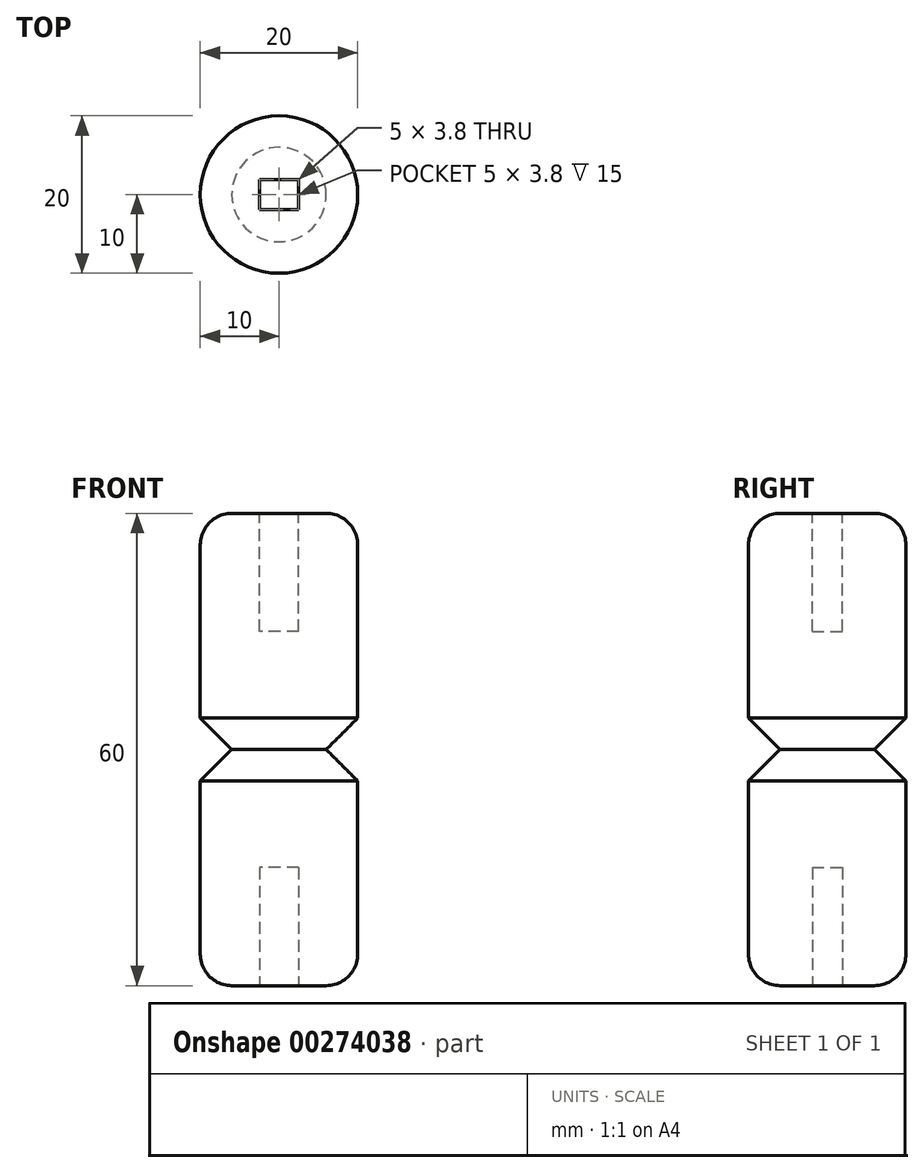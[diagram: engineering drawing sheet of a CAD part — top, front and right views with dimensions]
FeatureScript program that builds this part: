
annotation { "Feature Type Name" : "Feature", "Feature Type Description" : "" }
export const myFeature = defineFeature(function(context is Context, id is Id, definition is map)
    precondition{}
    {
        {
            var Q0;
            Q0=qCreatedBy(makeId("Top.planeOp"),FACE);
            var sketch = newSketch(context, id + "F0", { "sketchPlane" : qUnion([Q0])});
            skCircle(sketch, "E0", {"center": v(0, 0) * mm, "radius": 10 * mm});
            skSolve(sketch);
        }
        {
            var Q0;
            Q0 = qSketchRegion(id + "F0", true);
            extrude(context, id + "F1", {"entities" : qUnion([Q0]), "depth" : 30 * mm});
        }
        {
            var Q0;
            Q0=makeQuery(id+"F1.opExtrude","CAP_FACE",FACE,{"disambiguationData":[OSD([sQuery(id+"F0.wireOp",EDGE,"E0")])],"isStart":false});
            var sketch = newSketch(context, id + "F2", { "sketchPlane" : qUnion([Q0])});
            skLineSegment(sketch, "E1.bottom", {"start": v(2.5, -1.9) * mm, "end": v(-2.5, -1.9) * mm});
            skLineSegment(sketch, "E1.top", {"start": v(2.5, 1.9) * mm, "end": v(-2.5, 1.9) * mm});
            skLineSegment(sketch, "E1.left", {"start": v(2.5, -1.9) * mm, "end": v(2.5, 1.9) * mm});
            skLineSegment(sketch, "E1.right", {"start": v(-2.5, -1.9) * mm, "end": v(-2.5, 1.9) * mm});
            skPoint(sketch, "E1.middle", {"position": v(0, 0) * mm});
            skSolve(sketch);
        }
        {
            var Q0;
            Q0 = qSketchRegion(id + "F2", true);
            extrude(context, id + "F3", {"entities" : qUnion([Q0]), "operationType" : NewBodyOperationType.REMOVE, "oppositeDirection" : true, "depth" : 15 * mm});
        }
        {
            var Q0;
            Q0=makeQuery(id+"F1.opExtrude","CAP_EDGE",EDGE,{"disambiguationData":[OSD([sQuery(id+"F0.wireOp",EDGE,"E0")])],"isStart":false});
            fillet(context, id + "F4", {"entities" : qUnion([Q0]), "radius" : 4 * mm, "tangentPropagation" : true, "allowEdgeOverflow" : false});
        }
        {
            var Q0;
            Q0=makeQuery(id+"F1.opExtrude","CAP_EDGE",EDGE,{"disambiguationData":[OSD([sQuery(id+"F0.wireOp",EDGE,"E0")])],"isStart":true});
            chamfer(context, id + "F5", {"entities" : qUnion([Q0]), "width" : 4 * mm, "tangentPropagation" : true});
        }
        {
            var Q0;
            Q0=makeQuery(id+"F1.opExtrude","SWEPT_BODY",BODY,{"disambiguationData":[OSD([sQuery(id+"F0.wireOp",EDGE,"E0")])]});
            var Q1;
            Q1=makeQuery(id+"F1.opExtrude","CAP_FACE",FACE,{"disambiguationData":[OSD([sQuery(id+"F0.wireOp",EDGE,"E0")])],"isStart":true});
            mirror(context, id + "F6", {"operationType" : NewBodyOperationType.ADD, "entities" : qUnion([Q0]), "mirrorPlane" : qUnion([Q1])});
        }
    });
